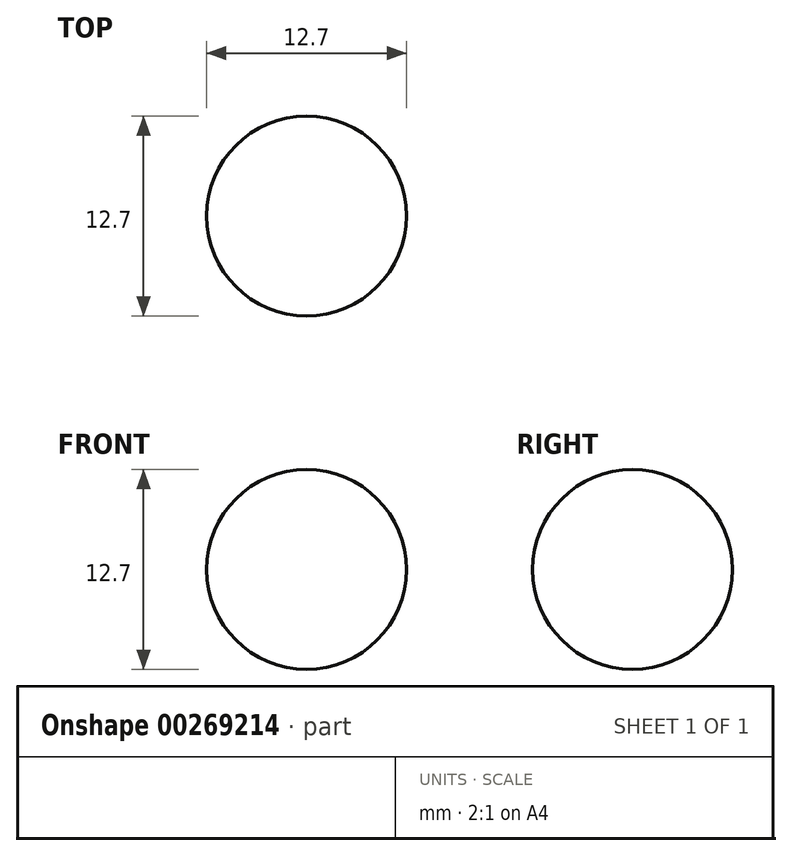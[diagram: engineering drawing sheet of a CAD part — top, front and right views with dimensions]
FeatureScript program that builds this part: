
annotation { "Feature Type Name" : "Feature", "Feature Type Description" : "" }
export const myFeature = defineFeature(function(context is Context, id is Id, definition is map)
    precondition{}
    {
        {
            var Q0;
            Q0=qCreatedBy(makeId("Front.planeOp"),FACE);
            var sketch = newSketch(context, id + "F0", { "sketchPlane" : qUnion([Q0])});
            skCircle(sketch, "E0", {"center": v(0, 0) * mm, "radius": 6.35 * mm});
            skLineSegment(sketch, "E1", {"start": v(-6.35, 0) * mm, "end": v(-6.35, 0) * mm});
            skLineSegment(sketch, "E2", {"start": v(0, -6.35) * mm, "end": v(0, -6.35) * mm});
            skLineSegment(sketch, "E3", {"start": v(-6.35, 0) * mm, "end": v(6.35, 0) * mm});
            skSolve(sketch);
        }
        {
            var Q0;
            {var subQ0=sQuery(id+"F0.wireOp",EDGE,"E3");Q0=makeQuery(id+"F0.imprint","IMPRINT",FACE,{"disambiguationData":[TD([[makeQuery(id+"F0.imprint","IMPRINT",EDGE,{"derivedFrom":subQ0}),1.0]])]});}
            var Q1;
            Q1=sQuery(id+"F0.wireOp",EDGE,"E3");
            revolve(context, id + "F1", {"entities" : qUnion([Q0]), "axis" : qUnion([Q1]), "revolveType" : RevolveType.FULL});
        }
    });
